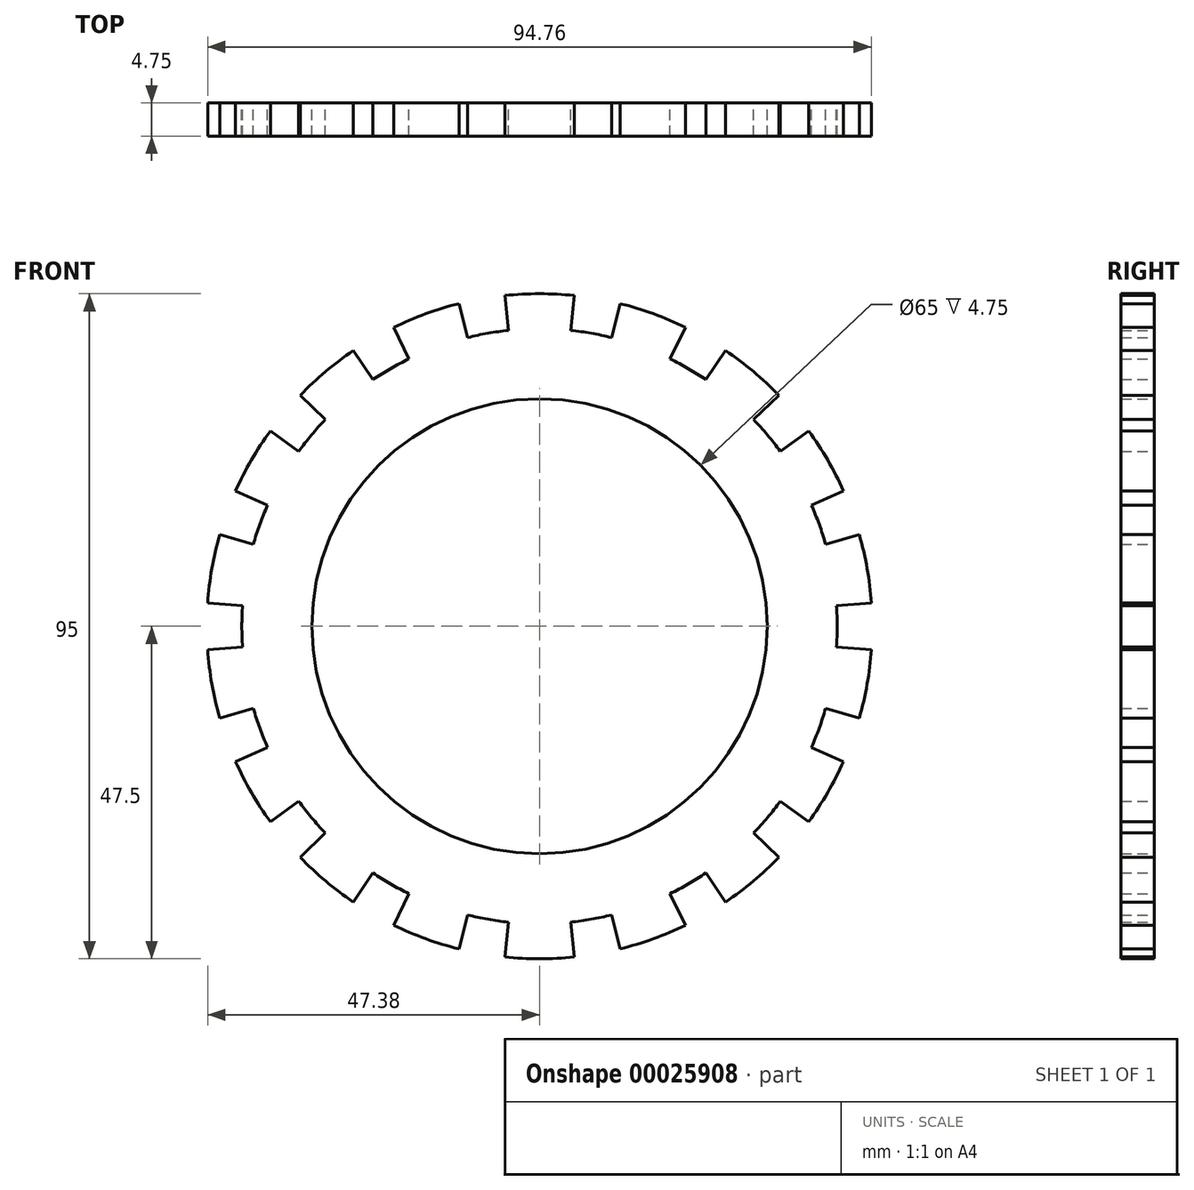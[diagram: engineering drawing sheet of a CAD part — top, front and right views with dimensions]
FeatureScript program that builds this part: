
annotation { "Feature Type Name" : "Feature", "Feature Type Description" : "" }
export const myFeature = defineFeature(function(context is Context, id is Id, definition is map)
    precondition{}
    {
        {
            var Q0;
            Q0=qCreatedBy(makeId("Front.planeOp"),FACE);
            var sketch = newSketch(context, id + "F0", { "sketchPlane" : qUnion([Q0])});
            skCircle(sketch, "E0", {"center": v(0, 0) * mm, "radius": 47.5 * mm, "construction": true});
            skCircle(sketch, "E1", {"center": v(0, 0) * mm, "radius": 42.5 * mm, "construction": true});
            skLineSegment(sketch, "E2", {"start": v(-4.97, 47.24) * mm, "end": v(0, 0) * mm, "construction": true});
            skLineSegment(sketch, "E3", {"start": v(0, 0) * mm, "end": v(-8.25, 46.78) * mm, "construction": true});
            skArc(sketch, "E4", {"start": v(-7.38, 41.85) * mm, "mid": v(-5.91, 42.09) * mm, "end": v(-4.44, 42.27) * mm});
            skLineSegment(sketch, "E5", {"start": v(-4.44, 42.27) * mm, "end": v(-4.97, 47.24) * mm});
            skArc(sketch, "E6", {"start": v(-4.97, 47.24) * mm, "mid": v(-2.49, 47.43) * mm, "end": v(0, 47.5) * mm});
            skArc(sketch, "E7.MirrorCS", {"start": v(4.97, 47.24) * mm, "mid": v(2.49, 47.43) * mm, "end": v(0, 47.5) * mm});
            skLineSegment(sketch, "E8.MirrorCS", {"start": v(4.44, 42.27) * mm, "end": v(4.97, 47.24) * mm});
            skArc(sketch, "E9.MirrorCS", {"start": v(7.38, 41.85) * mm, "mid": v(5.91, 42.09) * mm, "end": v(4.44, 42.27) * mm});
            skArc(sketch, "E10.1.0", {"start": v(-21.25, 36.8) * mm, "mid": v(-19.95, 37.53) * mm, "end": v(-18.63, 38.2) * mm});
            skLineSegment(sketch, "E10.1.1", {"start": v(-18.63, 38.2) * mm, "end": v(-20.82, 42.7) * mm});
            skArc(sketch, "E10.1.2", {"start": v(-20.82, 42.7) * mm, "mid": v(-18.56, 43.72) * mm, "end": v(-16.25, 44.64) * mm});
            skArc(sketch, "E10.1.3", {"start": v(-11.5, 46.09) * mm, "mid": v(-13.89, 45.42) * mm, "end": v(-16.25, 44.64) * mm});
            skLineSegment(sketch, "E10.1.4", {"start": v(-10.28, 41.24) * mm, "end": v(-11.5, 46.09) * mm});
            skArc(sketch, "E10.1.5", {"start": v(-7.38, 41.85) * mm, "mid": v(-8.84, 41.57) * mm, "end": v(-10.28, 41.24) * mm});
            skArc(sketch, "E10.2.0", {"start": v(-32.56, 27.32) * mm, "mid": v(-31.58, 28.44) * mm, "end": v(-30.57, 29.52) * mm});
            skLineSegment(sketch, "E10.2.1", {"start": v(-30.57, 29.52) * mm, "end": v(-34.17, 33) * mm});
            skArc(sketch, "E10.2.2", {"start": v(-34.17, 33) * mm, "mid": v(-32.4, 34.74) * mm, "end": v(-30.53, 36.39) * mm});
            skArc(sketch, "E10.2.3", {"start": v(-26.56, 39.38) * mm, "mid": v(-28.59, 37.94) * mm, "end": v(-30.53, 36.39) * mm});
            skLineSegment(sketch, "E10.2.4", {"start": v(-23.77, 35.23) * mm, "end": v(-26.56, 39.38) * mm});
            skArc(sketch, "E10.2.5", {"start": v(-21.25, 36.8) * mm, "mid": v(-22.52, 36.04) * mm, "end": v(-23.77, 35.23) * mm});
            skArc(sketch, "E10.3.0", {"start": v(-39.94, 14.54) * mm, "mid": v(-39.4, 15.92) * mm, "end": v(-38.83, 17.29) * mm});
            skLineSegment(sketch, "E10.3.1", {"start": v(-38.83, 17.29) * mm, "end": v(-43.4, 19.32) * mm});
            skArc(sketch, "E10.3.2", {"start": v(-43.4, 19.32) * mm, "mid": v(-42.32, 21.56) * mm, "end": v(-41.14, 23.75) * mm});
            skArc(sketch, "E10.3.3", {"start": v(-38.43, 27.92) * mm, "mid": v(-39.84, 25.87) * mm, "end": v(-41.14, 23.75) * mm});
            skLineSegment(sketch, "E10.3.4", {"start": v(-34.38, 24.98) * mm, "end": v(-38.43, 27.92) * mm});
            skArc(sketch, "E10.3.5", {"start": v(-32.56, 27.32) * mm, "mid": v(-33.5, 26.17) * mm, "end": v(-34.38, 24.98) * mm});
            skArc(sketch, "E10.4.0", {"start": v(-42.5, 0) * mm, "mid": v(-42.47, 1.48) * mm, "end": v(-42.4, 2.96) * mm});
            skLineSegment(sketch, "E10.4.1", {"start": v(-42.4, 2.96) * mm, "end": v(-47.38, 3.31) * mm});
            skArc(sketch, "E10.4.2", {"start": v(-47.38, 3.31) * mm, "mid": v(-47.15, 5.79) * mm, "end": v(-46.78, 8.25) * mm});
            skArc(sketch, "E10.4.3", {"start": v(-45.66, 13.1) * mm, "mid": v(-46.28, 10.69) * mm, "end": v(-46.78, 8.25) * mm});
            skLineSegment(sketch, "E10.4.4", {"start": v(-40.85, 11.71) * mm, "end": v(-45.66, 13.1) * mm});
            skArc(sketch, "E10.4.5", {"start": v(-39.94, 14.54) * mm, "mid": v(-40.42, 13.13) * mm, "end": v(-40.85, 11.71) * mm});
            skArc(sketch, "E10.5.0", {"start": v(-39.94, -14.54) * mm, "mid": v(-40.42, -13.13) * mm, "end": v(-40.85, -11.71) * mm});
            skLineSegment(sketch, "E10.5.1", {"start": v(-40.85, -11.71) * mm, "end": v(-45.66, -13.1) * mm});
            skArc(sketch, "E10.5.2", {"start": v(-45.66, -13.1) * mm, "mid": v(-46.28, -10.69) * mm, "end": v(-46.78, -8.25) * mm});
            skArc(sketch, "E10.5.3", {"start": v(-47.38, -3.31) * mm, "mid": v(-47.15, -5.79) * mm, "end": v(-46.78, -8.25) * mm});
            skLineSegment(sketch, "E10.5.4", {"start": v(-42.4, -2.96) * mm, "end": v(-47.38, -3.31) * mm});
            skArc(sketch, "E10.5.5", {"start": v(-42.5, 0) * mm, "mid": v(-42.47, -1.48) * mm, "end": v(-42.4, -2.96) * mm});
            skArc(sketch, "E10.6.0", {"start": v(-32.56, -27.32) * mm, "mid": v(-33.5, -26.17) * mm, "end": v(-34.38, -24.98) * mm});
            skLineSegment(sketch, "E10.6.1", {"start": v(-34.38, -24.98) * mm, "end": v(-38.43, -27.92) * mm});
            skArc(sketch, "E10.6.2", {"start": v(-38.43, -27.92) * mm, "mid": v(-39.84, -25.87) * mm, "end": v(-41.14, -23.75) * mm});
            skArc(sketch, "E10.6.3", {"start": v(-43.4, -19.32) * mm, "mid": v(-42.32, -21.56) * mm, "end": v(-41.14, -23.75) * mm});
            skLineSegment(sketch, "E10.6.4", {"start": v(-38.83, -17.29) * mm, "end": v(-43.4, -19.32) * mm});
            skArc(sketch, "E10.6.5", {"start": v(-39.94, -14.54) * mm, "mid": v(-39.4, -15.92) * mm, "end": v(-38.83, -17.29) * mm});
            skArc(sketch, "E10.7.0", {"start": v(-21.25, -36.8) * mm, "mid": v(-22.52, -36.04) * mm, "end": v(-23.77, -35.23) * mm});
            skLineSegment(sketch, "E10.7.1", {"start": v(-23.77, -35.23) * mm, "end": v(-26.56, -39.38) * mm});
            skArc(sketch, "E10.7.2", {"start": v(-26.56, -39.38) * mm, "mid": v(-28.59, -37.94) * mm, "end": v(-30.53, -36.39) * mm});
            skArc(sketch, "E10.7.3", {"start": v(-34.17, -33) * mm, "mid": v(-32.4, -34.74) * mm, "end": v(-30.53, -36.39) * mm});
            skLineSegment(sketch, "E10.7.4", {"start": v(-30.57, -29.52) * mm, "end": v(-34.17, -33) * mm});
            skArc(sketch, "E10.7.5", {"start": v(-32.56, -27.32) * mm, "mid": v(-31.58, -28.44) * mm, "end": v(-30.57, -29.52) * mm});
            skArc(sketch, "E10.8.0", {"start": v(-7.38, -41.85) * mm, "mid": v(-8.84, -41.57) * mm, "end": v(-10.28, -41.24) * mm});
            skLineSegment(sketch, "E10.8.1", {"start": v(-10.28, -41.24) * mm, "end": v(-11.5, -46.09) * mm});
            skArc(sketch, "E10.8.2", {"start": v(-11.5, -46.09) * mm, "mid": v(-13.89, -45.42) * mm, "end": v(-16.25, -44.64) * mm});
            skArc(sketch, "E10.8.3", {"start": v(-20.82, -42.7) * mm, "mid": v(-18.56, -43.72) * mm, "end": v(-16.25, -44.64) * mm});
            skLineSegment(sketch, "E10.8.4", {"start": v(-18.63, -38.2) * mm, "end": v(-20.82, -42.7) * mm});
            skArc(sketch, "E10.8.5", {"start": v(-21.25, -36.8) * mm, "mid": v(-19.95, -37.53) * mm, "end": v(-18.63, -38.2) * mm});
            skArc(sketch, "E10.9.0", {"start": v(7.38, -41.85) * mm, "mid": v(5.91, -42.09) * mm, "end": v(4.44, -42.27) * mm});
            skLineSegment(sketch, "E10.9.1", {"start": v(4.44, -42.27) * mm, "end": v(4.97, -47.24) * mm});
            skArc(sketch, "E10.9.2", {"start": v(4.97, -47.24) * mm, "mid": v(2.49, -47.43) * mm, "end": v(0, -47.5) * mm});
            skArc(sketch, "E10.9.3", {"start": v(-4.97, -47.24) * mm, "mid": v(-2.49, -47.43) * mm, "end": v(0, -47.5) * mm});
            skLineSegment(sketch, "E10.9.4", {"start": v(-4.44, -42.27) * mm, "end": v(-4.97, -47.24) * mm});
            skArc(sketch, "E10.9.5", {"start": v(-7.38, -41.85) * mm, "mid": v(-5.91, -42.09) * mm, "end": v(-4.44, -42.27) * mm});
            skArc(sketch, "E10.10.0", {"start": v(21.25, -36.8) * mm, "mid": v(19.95, -37.53) * mm, "end": v(18.63, -38.2) * mm});
            skLineSegment(sketch, "E10.10.1", {"start": v(18.63, -38.2) * mm, "end": v(20.82, -42.7) * mm});
            skArc(sketch, "E10.10.2", {"start": v(20.82, -42.7) * mm, "mid": v(18.56, -43.72) * mm, "end": v(16.25, -44.64) * mm});
            skArc(sketch, "E10.10.3", {"start": v(11.5, -46.09) * mm, "mid": v(13.89, -45.42) * mm, "end": v(16.25, -44.64) * mm});
            skLineSegment(sketch, "E10.10.4", {"start": v(10.28, -41.24) * mm, "end": v(11.5, -46.09) * mm});
            skArc(sketch, "E10.10.5", {"start": v(7.38, -41.85) * mm, "mid": v(8.84, -41.57) * mm, "end": v(10.28, -41.24) * mm});
            skArc(sketch, "E10.11.0", {"start": v(32.56, -27.32) * mm, "mid": v(31.58, -28.44) * mm, "end": v(30.57, -29.52) * mm});
            skLineSegment(sketch, "E10.11.1", {"start": v(30.57, -29.52) * mm, "end": v(34.17, -33) * mm});
            skArc(sketch, "E10.11.2", {"start": v(34.17, -33) * mm, "mid": v(32.4, -34.74) * mm, "end": v(30.53, -36.39) * mm});
            skArc(sketch, "E10.11.3", {"start": v(26.56, -39.38) * mm, "mid": v(28.59, -37.94) * mm, "end": v(30.53, -36.39) * mm});
            skLineSegment(sketch, "E10.11.4", {"start": v(23.77, -35.23) * mm, "end": v(26.56, -39.38) * mm});
            skArc(sketch, "E10.11.5", {"start": v(21.25, -36.8) * mm, "mid": v(22.52, -36.04) * mm, "end": v(23.77, -35.23) * mm});
            skArc(sketch, "E10.12.0", {"start": v(39.94, -14.54) * mm, "mid": v(39.4, -15.92) * mm, "end": v(38.83, -17.29) * mm});
            skLineSegment(sketch, "E10.12.1", {"start": v(38.83, -17.29) * mm, "end": v(43.4, -19.32) * mm});
            skArc(sketch, "E10.12.2", {"start": v(43.4, -19.32) * mm, "mid": v(42.32, -21.56) * mm, "end": v(41.14, -23.75) * mm});
            skArc(sketch, "E10.12.3", {"start": v(38.43, -27.92) * mm, "mid": v(39.84, -25.87) * mm, "end": v(41.14, -23.75) * mm});
            skLineSegment(sketch, "E10.12.4", {"start": v(34.38, -24.98) * mm, "end": v(38.43, -27.92) * mm});
            skArc(sketch, "E10.12.5", {"start": v(32.56, -27.32) * mm, "mid": v(33.5, -26.17) * mm, "end": v(34.38, -24.98) * mm});
            skArc(sketch, "E10.13.0", {"start": v(42.5, 0) * mm, "mid": v(42.47, -1.48) * mm, "end": v(42.4, -2.96) * mm});
            skLineSegment(sketch, "E10.13.1", {"start": v(42.4, -2.96) * mm, "end": v(47.38, -3.31) * mm});
            skArc(sketch, "E10.13.2", {"start": v(47.38, -3.31) * mm, "mid": v(47.15, -5.79) * mm, "end": v(46.78, -8.25) * mm});
            skArc(sketch, "E10.13.3", {"start": v(45.66, -13.1) * mm, "mid": v(46.28, -10.69) * mm, "end": v(46.78, -8.25) * mm});
            skLineSegment(sketch, "E10.13.4", {"start": v(40.85, -11.71) * mm, "end": v(45.66, -13.1) * mm});
            skArc(sketch, "E10.13.5", {"start": v(39.94, -14.54) * mm, "mid": v(40.42, -13.13) * mm, "end": v(40.85, -11.71) * mm});
            skArc(sketch, "E10.14.0", {"start": v(39.94, 14.54) * mm, "mid": v(40.42, 13.13) * mm, "end": v(40.85, 11.71) * mm});
            skLineSegment(sketch, "E10.14.1", {"start": v(40.85, 11.71) * mm, "end": v(45.66, 13.1) * mm});
            skArc(sketch, "E10.14.2", {"start": v(45.66, 13.1) * mm, "mid": v(46.28, 10.69) * mm, "end": v(46.78, 8.25) * mm});
            skArc(sketch, "E10.14.3", {"start": v(47.38, 3.31) * mm, "mid": v(47.15, 5.79) * mm, "end": v(46.78, 8.25) * mm});
            skLineSegment(sketch, "E10.14.4", {"start": v(42.4, 2.96) * mm, "end": v(47.38, 3.31) * mm});
            skArc(sketch, "E10.14.5", {"start": v(42.5, 0) * mm, "mid": v(42.47, 1.48) * mm, "end": v(42.4, 2.96) * mm});
            skArc(sketch, "E10.15.0", {"start": v(32.56, 27.32) * mm, "mid": v(33.5, 26.17) * mm, "end": v(34.38, 24.98) * mm});
            skLineSegment(sketch, "E10.15.1", {"start": v(34.38, 24.98) * mm, "end": v(38.43, 27.92) * mm});
            skArc(sketch, "E10.15.2", {"start": v(38.43, 27.92) * mm, "mid": v(39.84, 25.87) * mm, "end": v(41.14, 23.75) * mm});
            skArc(sketch, "E10.15.3", {"start": v(43.4, 19.32) * mm, "mid": v(42.32, 21.56) * mm, "end": v(41.14, 23.75) * mm});
            skLineSegment(sketch, "E10.15.4", {"start": v(38.83, 17.29) * mm, "end": v(43.4, 19.32) * mm});
            skArc(sketch, "E10.15.5", {"start": v(39.94, 14.54) * mm, "mid": v(39.4, 15.92) * mm, "end": v(38.83, 17.29) * mm});
            skArc(sketch, "E10.16.0", {"start": v(21.25, 36.8) * mm, "mid": v(22.52, 36.04) * mm, "end": v(23.77, 35.23) * mm});
            skLineSegment(sketch, "E10.16.1", {"start": v(23.77, 35.23) * mm, "end": v(26.56, 39.38) * mm});
            skArc(sketch, "E10.16.2", {"start": v(26.56, 39.38) * mm, "mid": v(28.59, 37.94) * mm, "end": v(30.53, 36.39) * mm});
            skArc(sketch, "E10.16.3", {"start": v(34.17, 33) * mm, "mid": v(32.4, 34.74) * mm, "end": v(30.53, 36.39) * mm});
            skLineSegment(sketch, "E10.16.4", {"start": v(30.57, 29.52) * mm, "end": v(34.17, 33) * mm});
            skArc(sketch, "E10.16.5", {"start": v(32.56, 27.32) * mm, "mid": v(31.58, 28.44) * mm, "end": v(30.57, 29.52) * mm});
            skArc(sketch, "E10.17.0", {"start": v(7.38, 41.85) * mm, "mid": v(8.84, 41.57) * mm, "end": v(10.28, 41.24) * mm});
            skLineSegment(sketch, "E10.17.1", {"start": v(10.28, 41.24) * mm, "end": v(11.5, 46.09) * mm});
            skArc(sketch, "E10.17.2", {"start": v(11.5, 46.09) * mm, "mid": v(13.89, 45.42) * mm, "end": v(16.25, 44.64) * mm});
            skArc(sketch, "E10.17.3", {"start": v(20.82, 42.7) * mm, "mid": v(18.56, 43.72) * mm, "end": v(16.25, 44.64) * mm});
            skLineSegment(sketch, "E10.17.4", {"start": v(18.63, 38.2) * mm, "end": v(20.82, 42.7) * mm});
            skArc(sketch, "E10.17.5", {"start": v(21.25, 36.8) * mm, "mid": v(19.95, 37.53) * mm, "end": v(18.63, 38.2) * mm});
            skCircle(sketch, "E11", {"center": v(0, 0) * mm, "radius": 32.5 * mm});
            skSolve(sketch);
        }
        {
            var Q0;
            Q0=qSketchRegion(id+"F0",true);
            extrude(context, id + "F1", {"entities" : qUnion([Q0]), "depth" : 4.75 * mm});
        }
    });
